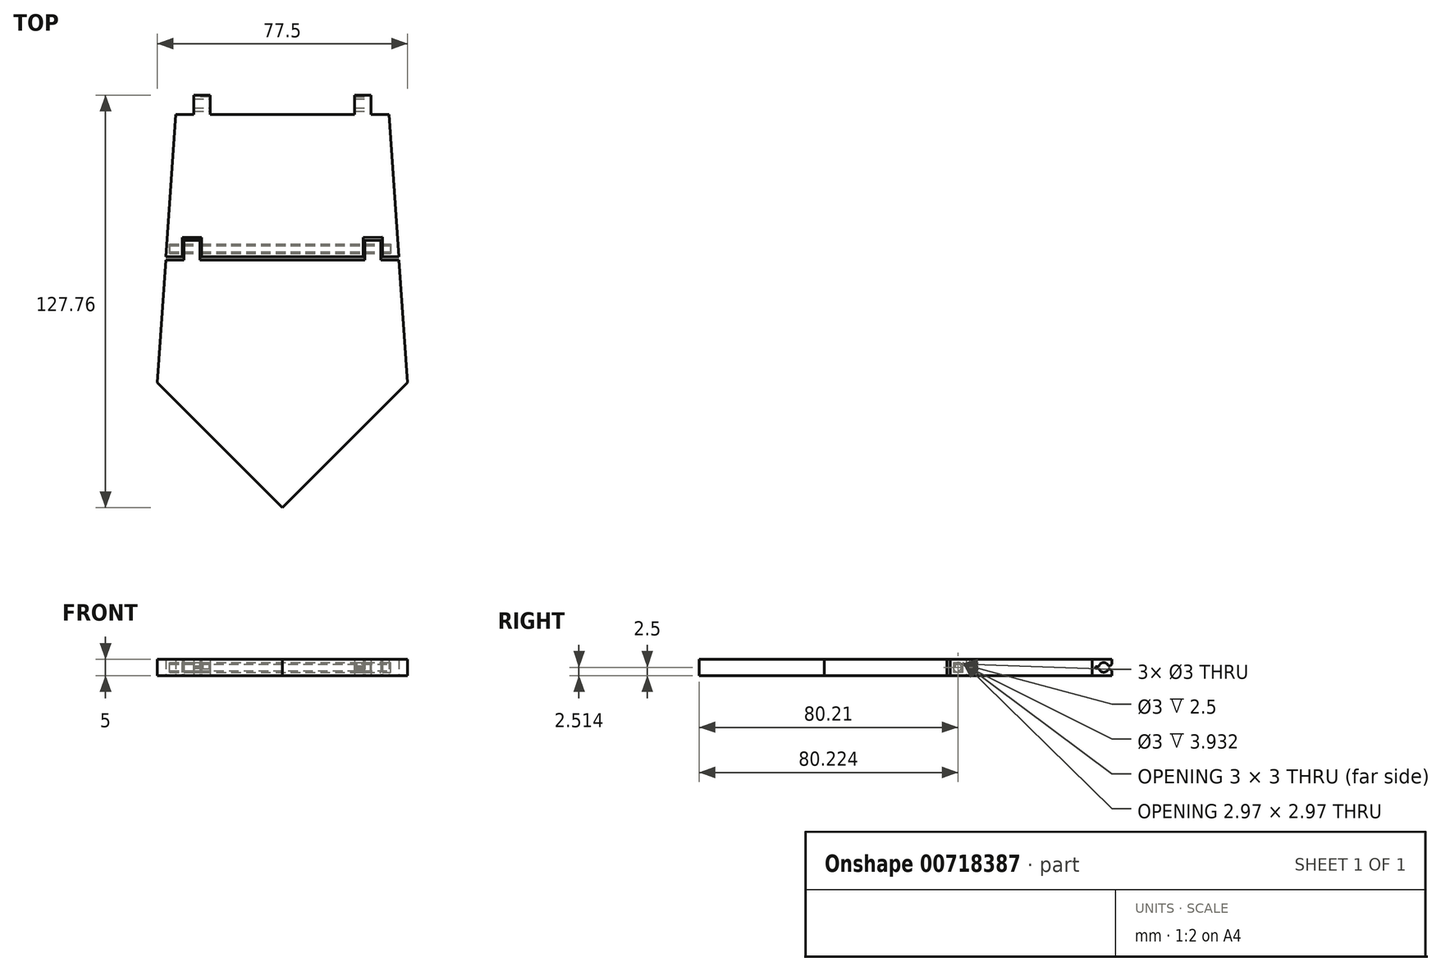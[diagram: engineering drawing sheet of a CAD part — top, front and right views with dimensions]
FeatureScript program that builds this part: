
annotation { "Feature Type Name" : "Feature", "Feature Type Description" : "" }
export const myFeature = defineFeature(function(context is Context, id is Id, definition is map)
    precondition{}
    {
        {
            var Q0;
            Q0=qCreatedBy(makeId("Top.planeOp"),FACE);
            var sketch = newSketch(context, id + "F0", { "sketchPlane" : qUnion([Q0])});
            skLineSegment(sketch, "E0", {"start": v(-38.75, -56.1) * mm, "end": v(0.02, -94.87) * mm});
            skLineSegment(sketch, "E1", {"start": v(0.02, -94.87) * mm, "end": v(38.75, -56.15) * mm});
            skLineSegment(sketch, "E2.left", {"start": v(-31.03, -17.1) * mm, "end": v(-31.03, -11.1) * mm});
            skLineSegment(sketch, "E2.right", {"start": v(-25.03, -17.1) * mm, "end": v(-25.03, -11.1) * mm});
            skLineSegment(sketch, "E3", {"start": v(-36.03, -17.1) * mm, "end": v(-31.03, -17.1) * mm});
            skLineSegment(sketch, "E4", {"start": v(-31.03, -11.1) * mm, "end": v(-25.03, -11.1) * mm});
            skLineSegment(sketch, "E5.MirrorCS", {"start": v(31.03, -11.09) * mm, "end": v(25.03, -11.1) * mm});
            skLineSegment(sketch, "E6.MirrorCS", {"start": v(25.03, -17.1) * mm, "end": v(25.03, -11.1) * mm});
            skLineSegment(sketch, "E7.MirrorCS", {"start": v(31.03, -17.1) * mm, "end": v(31.03, -11.09) * mm});
            skLineSegment(sketch, "E8", {"start": v(-32.97, 26.9) * mm, "end": v(-27.4, 26.9) * mm});
            skLineSegment(sketch, "E9", {"start": v(-36.1, -18.1) * mm, "end": v(-30.53, -18.1) * mm});
            skLineSegment(sketch, "E10.top", {"start": v(-27.4, 32.9) * mm, "end": v(-22.4, 32.9) * mm});
            skLineSegment(sketch, "E10.left", {"start": v(-27.4, 26.9) * mm, "end": v(-27.4, 32.9) * mm});
            skLineSegment(sketch, "E10.right", {"start": v(-22.4, 26.9) * mm, "end": v(-22.4, 32.9) * mm});
            skLineSegment(sketch, "E11.top", {"start": v(-30.53, -12.1) * mm, "end": v(-25.53, -12.1) * mm});
            skLineSegment(sketch, "E11.left", {"start": v(-30.53, -18.1) * mm, "end": v(-30.53, -12.1) * mm});
            skLineSegment(sketch, "E11.right", {"start": v(-25.53, -18.1) * mm, "end": v(-25.53, -12.1) * mm});
            skLineSegment(sketch, "E12.MirrorCS", {"start": v(27.4, 26.9) * mm, "end": v(27.4, 32.9) * mm});
            skLineSegment(sketch, "E13.MirrorCS", {"start": v(27.4, 32.9) * mm, "end": v(22.4, 32.9) * mm});
            skLineSegment(sketch, "E14.MirrorCS", {"start": v(22.4, 26.9) * mm, "end": v(22.4, 32.9) * mm});
            skLineSegment(sketch, "E15.MirrorCS", {"start": v(30.53, -18.15) * mm, "end": v(30.53, -12.1) * mm});
            skLineSegment(sketch, "E16.MirrorCS", {"start": v(30.53, -12.1) * mm, "end": v(25.53, -12.1) * mm});
            skLineSegment(sketch, "E17.trimOffspring", {"start": v(-32.97, 26.9) * mm, "end": v(-36.03, -17.1) * mm});
            skLineSegment(sketch, "E18.trimOffspring", {"start": v(-22.4, 26.9) * mm, "end": v(22.4, 26.9) * mm});
            skLineSegment(sketch, "E19.trimOffspring", {"start": v(27.4, 26.9) * mm, "end": v(32.97, 26.9) * mm});
            skLineSegment(sketch, "E20.trimOffspring", {"start": v(32.97, 26.9) * mm, "end": v(36.03, -17.1) * mm});
            skLineSegment(sketch, "E21.trimOffspring", {"start": v(-36.1, -18.1) * mm, "end": v(-38.75, -56.1) * mm});
            skLineSegment(sketch, "E22.trimOffspring", {"start": v(-25.03, -17.1) * mm, "end": v(25.03, -17.1) * mm});
            skLineSegment(sketch, "E23.trimOffspring", {"start": v(31.03, -17.1) * mm, "end": v(36.03, -17.1) * mm});
            skLineSegment(sketch, "E24.trimOffspring", {"start": v(30.53, -18.15) * mm, "end": v(36.1, -18.15) * mm});
            skLineSegment(sketch, "E25.trimOffspring", {"start": v(36.1, -18.15) * mm, "end": v(38.75, -56.15) * mm});
            skLineSegment(sketch, "E26", {"start": v(25.53, -12.1) * mm, "end": v(25.53, -18.1) * mm});
            skLineSegment(sketch, "E27", {"start": v(25.53, -18.1) * mm, "end": v(-25.53, -18.1) * mm});
            skLineSegment(sketch, "E28.trimOffspring", {"start": v(25.53, -17.1) * mm, "end": v(25.54, -17.1) * mm});
            skSolve(sketch);
        }
        {
            var Q0;
            Q0 = qSketchRegion(id + "F0", true);
            extrude(context, id + "F1", {"entities" : qUnion([Q0]), "depth" : 5 * mm, "offsetDistance" : 25 * mm});
        }
        {
            var Q0;
            Q0=makeQuery(id+"F1.opExtrude","SWEPT_FACE",FACE,{"disambiguationData":[OSD([sQuery(id+"F0.wireOp",EDGE,"E12.MirrorCS")])]});
            cPlane(context, id + "F2", {"entities" : qUnion([Q0]), "cplaneType" : CPlaneType.OFFSET, "offset" : 10 * mm, "width" : 150 * mm, "height" : 150 * mm});
        }
        {
            var Q0;
            Q0=qCreatedBy(id+"F2.planeOp",FACE);
            var sketch = newSketch(context, id + "F3", { "sketchPlane" : qUnion([Q0])});
            skArc(sketch, "E29", {"start": v(31.8, 3) * mm, "mid": v(30.26, 4) * mm, "end": v(28.91, 2.75) * mm});
            skLineSegment(sketch, "E30.bottom", {"start": v(34.77, 3) * mm, "end": v(31.8, 3) * mm});
            skLineSegment(sketch, "E30.top", {"start": v(34.77, 2) * mm, "end": v(31.8, 2) * mm});
            skLineSegment(sketch, "E30.left", {"start": v(34.77, 3) * mm, "end": v(34.77, 2) * mm});
            skPoint(sketch, "E31.orphan", {"position": v(30.4, 2) * mm});
            skLineSegment(sketch, "E32.bottom", {"start": v(28.91, 2.75) * mm, "end": v(27.9, 2.75) * mm});
            skLineSegment(sketch, "E32.top", {"start": v(28.91, 2.25) * mm, "end": v(27.9, 2.25) * mm});
            skLineSegment(sketch, "E32.right", {"start": v(27.9, 2.75) * mm, "end": v(27.9, 2.25) * mm});
            skArc(sketch, "E33.trimOffspring", {"start": v(28.91, 2.25) * mm, "mid": v(30.26, 1) * mm, "end": v(31.8, 2) * mm});
            skSolve(sketch);
        }
        {
            var Q0;
            Q0 = qSketchRegion(id + "F3", true);
            extrude(context, id + "F4", {"entities" : qUnion([Q0]), "operationType" : NewBodyOperationType.REMOVE, "oppositeDirection" : true, "depth" : 72.8 * mm, "offsetDistance" : 25 * mm});
        }
        {
            var Q0;
            Q0=makeQuery(id+"F4.boolean.opBoolean","INTERSECT",EDGE,{"derivedFrom":[makeQuery(id+"F1.opExtrude","SWEPT_FACE",FACE,{"disambiguationData":[OSD([sQuery(id+"F0.wireOp",EDGE,"E13.MirrorCS")])]}),makeQuery(id+"F4.opExtrude","SWEPT_FACE",FACE,{"disambiguationData":[OSD([sQuery(id+"F3.wireOp",EDGE,"E30.bottom")])]})]});
            var Q1;
            Q1=makeQuery(id+"F4.boolean.opBoolean","INTERSECT",EDGE,{"derivedFrom":[makeQuery(id+"F1.opExtrude","SWEPT_FACE",FACE,{"disambiguationData":[OSD([sQuery(id+"F0.wireOp",EDGE,"E13.MirrorCS")])]}),makeQuery(id+"F4.opExtrude","SWEPT_FACE",FACE,{"disambiguationData":[OSD([sQuery(id+"F3.wireOp",EDGE,"E30.top")])]})]});
            var Q2;
            Q2=makeQuery(id+"F4.boolean.opBoolean","INTERSECT",EDGE,{"derivedFrom":[makeQuery(id+"F1.opExtrude","SWEPT_FACE",FACE,{"disambiguationData":[OSD([sQuery(id+"F0.wireOp",EDGE,"E10.top")])]}),makeQuery(id+"F4.opExtrude","SWEPT_FACE",FACE,{"disambiguationData":[OSD([sQuery(id+"F3.wireOp",EDGE,"E30.bottom")])]})]});
            var Q3;
            Q3=makeQuery(id+"F4.boolean.opBoolean","INTERSECT",EDGE,{"derivedFrom":[makeQuery(id+"F1.opExtrude","SWEPT_FACE",FACE,{"disambiguationData":[OSD([sQuery(id+"F0.wireOp",EDGE,"E10.top")])]}),makeQuery(id+"F4.opExtrude","SWEPT_FACE",FACE,{"disambiguationData":[OSD([sQuery(id+"F3.wireOp",EDGE,"E30.top")])]})]});
            chamfer(context, id + "F5", {"entities" : qUnion([Q0, Q1, Q2, Q3]), "width" : 0.5 * mm, "tangentPropagation" : true});
        }
        {
            var Q0;
            Q0=makeQuery(id+"F1.opExtrude","SWEPT_FACE",FACE,{"disambiguationData":[OSD([sQuery(id+"F0.wireOp",EDGE,"E15.MirrorCS")])]});
            cPlane(context, id + "F6", {"entities" : qUnion([Q0]), "cplaneType" : CPlaneType.OFFSET, "offset" : 10 * mm, "width" : 150 * mm, "height" : 150 * mm});
        }
        {
            var Q0;
            Q0=qCreatedBy(id+"F6.planeOp",FACE);
            var sketch = newSketch(context, id + "F7", { "sketchPlane" : qUnion([Q0])});
            skCircle(sketch, "E34", {"center": v(-14.65, 2.5) * mm, "radius": 1.5 * mm});
            skCircle(sketch, "E35", {"center": v(-14.65, 2.5) * mm, "radius": 1 * mm});
            skSolve(sketch);
        }
        {
            var Q0;
            Q0 = qSketchRegion(id + "F7", true);
            extrude(context, id + "F8", {"entities" : qUnion([Q0]), "operationType" : NewBodyOperationType.REMOVE, "oppositeDirection" : true, "depth" : 75.5 * mm, "offsetDistance" : 25 * mm, "hasSecondDirection" : true, "secondDirectionOppositeDirection" : true, "secondDirectionDepth" : 7 * mm});
        }
        {
            var Q0;
            Q0=makeQuery(id+"F7.imprint","IMPRINT",FACE,{"disambiguationData":[TD([[makeQuery(id+"F7.imprint","IMPRINT",EDGE,{"derivedFrom":sQuery(id+"F7.wireOp",EDGE,"E35")}),1.0]])]});
            extrude(context, id + "F9", {"entities" : qUnion([Q0]), "operationType" : NewBodyOperationType.ADD, "oppositeDirection" : true, "depth" : 74.3 * mm, "offsetDistance" : 25 * mm, "hasSecondDirection" : true, "secondDirectionOppositeDirection" : true, "secondDirectionDepth" : 5.6 * mm});
        }
    });
